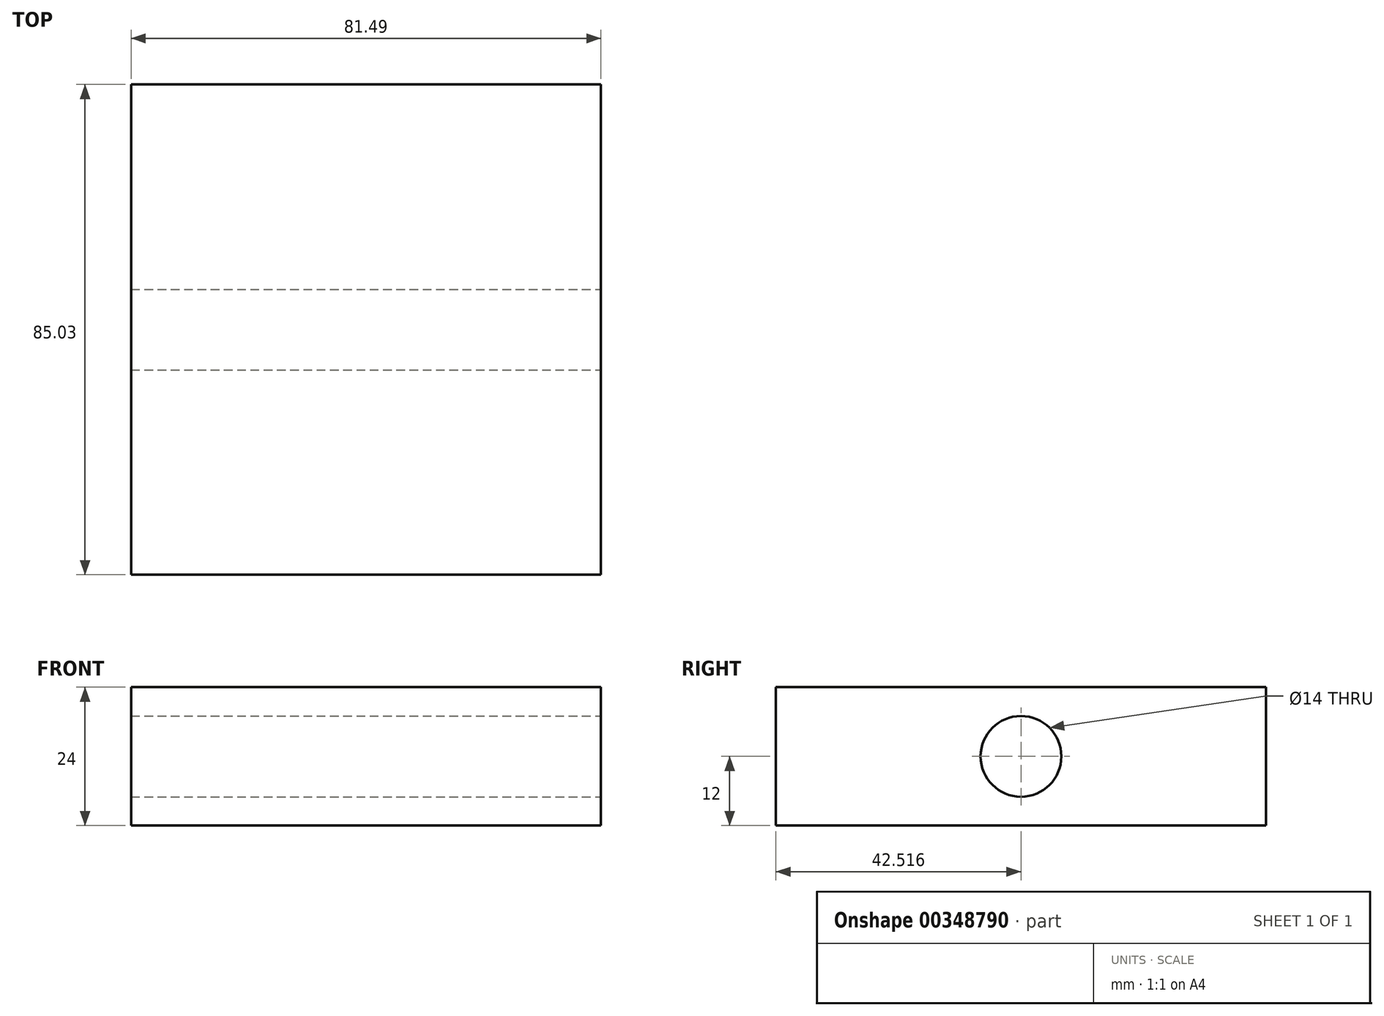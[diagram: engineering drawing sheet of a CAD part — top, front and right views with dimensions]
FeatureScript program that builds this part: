
annotation { "Feature Type Name" : "Feature", "Feature Type Description" : "" }
export const myFeature = defineFeature(function(context is Context, id is Id, definition is map)
    precondition{}
    {
        {
            var Q0;
            Q0=qCreatedBy(makeId("Top.planeOp"),FACE);
            var sketch = newSketch(context, id + "F0", { "sketchPlane" : qUnion([Q0])});
            skLineSegment(sketch, "E0.bottom", {"start": v(-36.4, 38.81) * mm, "end": v(45.1, 38.81) * mm});
            skLineSegment(sketch, "E0.top", {"start": v(-36.4, -46.22) * mm, "end": v(45.1, -46.22) * mm});
            skLineSegment(sketch, "E0.left", {"start": v(-36.4, 38.81) * mm, "end": v(-36.4, -46.22) * mm});
            skLineSegment(sketch, "E0.right", {"start": v(45.1, 38.81) * mm, "end": v(45.1, -46.22) * mm});
            skSolve(sketch);
        }
        {
            var Q0;
            Q0=makeQuery(id+"F0.imprint","IMPRINT",FACE,{"disambiguationData":[TD([[makeQuery(id+"F0.imprint","IMPRINT",EDGE,{"derivedFrom":sQuery(id+"F0.wireOp",EDGE,"E0.bottom")}),-1.0]])]});
            extrude(context, id + "F1", {"entities" : qUnion([Q0]), "depth" : 24 * mm});
        }
        {
            var Q0;
            Q0=makeQuery(id+"F1.opExtrude","SWEPT_FACE",FACE,{"disambiguationData":[OSD([sQuery(id+"F0.wireOp",EDGE,"E0.right")])]});
            var sketch = newSketch(context, id + "F2", { "sketchPlane" : qUnion([Q0])});
            skCircle(sketch, "E1", {"center": v(-3.7, 12) * mm, "radius": 7 * mm});
            skLineSegment(sketch, "E2", {"start": v(-40.43, 12) * mm, "end": v(51.39, 12) * mm, "construction": true});
            skLineSegment(sketch, "E3", {"start": v(-3.7, 29.29) * mm, "end": v(-3.7, -17.65) * mm, "construction": true});
            skSolve(sketch);
        }
        {
            var Q0;
            Q0=makeQuery(id+"F2.imprint","IMPRINT",FACE,{"disambiguationData":[TD([[makeQuery(id+"F2.imprint","IMPRINT",EDGE,{"derivedFrom":sQuery(id+"F2.wireOp",EDGE,"E1")}),1.0]])]});
            extrude(context, id + "F3", {"entities" : qUnion([Q0]), "operationType" : NewBodyOperationType.REMOVE, "endBound" : BoundingType.THROUGH_ALL, "oppositeDirection" : true, "depth" : 25 * mm});
        }
    });
